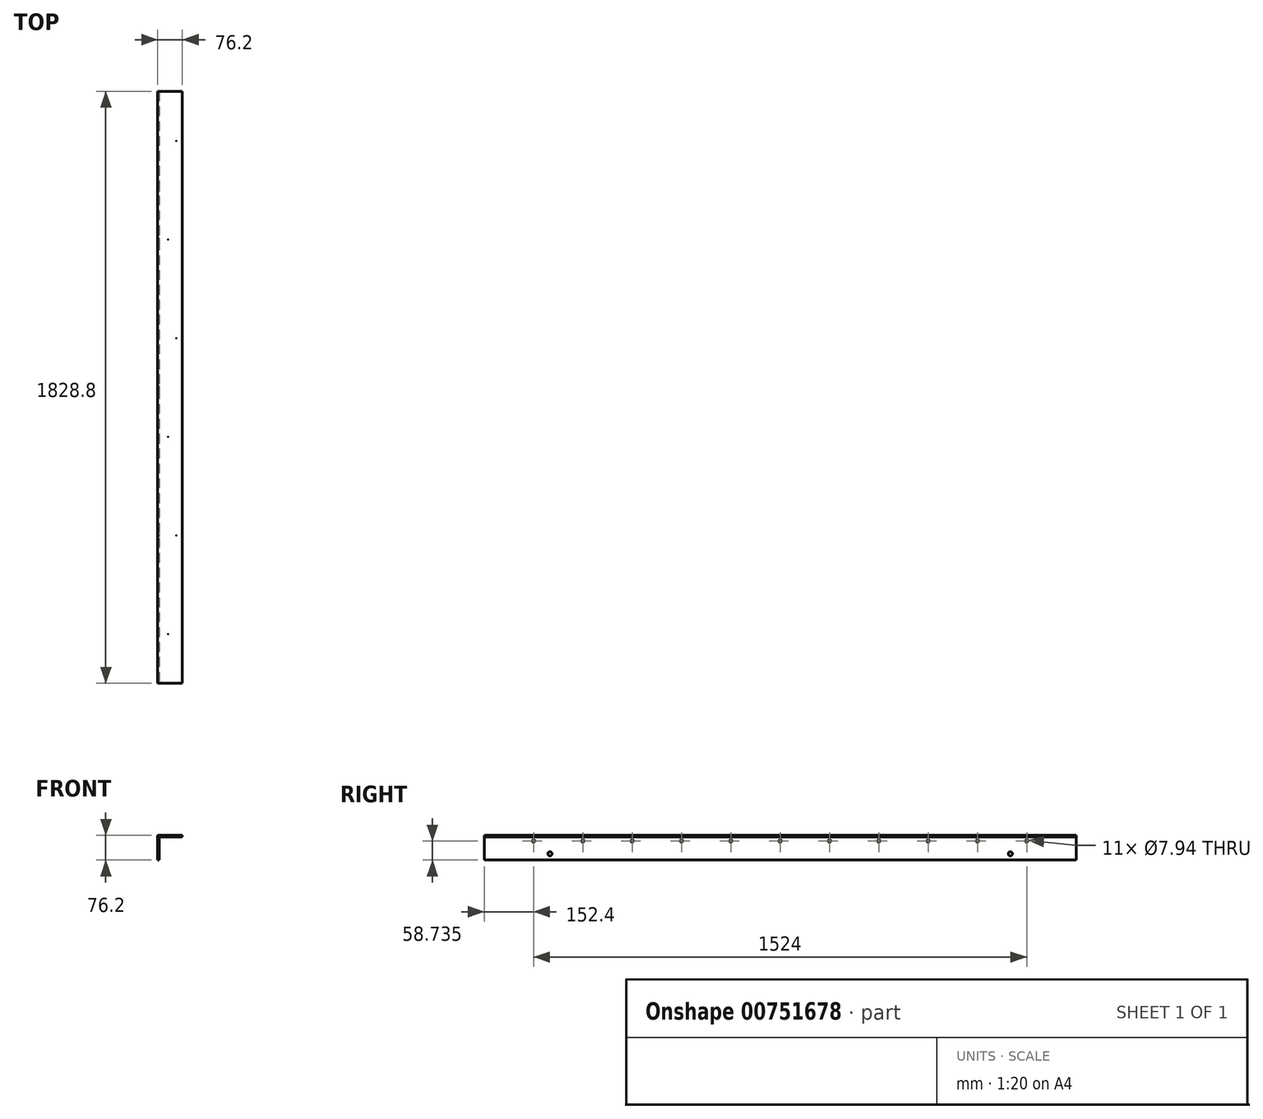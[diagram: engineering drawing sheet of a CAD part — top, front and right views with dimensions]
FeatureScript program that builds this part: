
annotation { "Feature Type Name" : "Feature", "Feature Type Description" : "" }
export const myFeature = defineFeature(function(context is Context, id is Id, definition is map)
    precondition{}
    {
        {
            var Q0;
            Q0=qCreatedBy(makeId("Front.planeOp"),FACE);
            var sketch = newSketch(context, id + "F0", { "sketchPlane" : qUnion([Q0])});
            skLineSegment(sketch, "E0", {"start": v(-59.9, 6.5) * mm, "end": v(16.3, 6.5) * mm});
            skLineSegment(sketch, "E1", {"start": v(16.3, 6.5) * mm, "end": v(16.3, 11.27) * mm});
            skLineSegment(sketch, "E2", {"start": v(16.3, 11.27) * mm, "end": v(-55.14, 11.27) * mm});
            skLineSegment(sketch, "E3", {"start": v(-55.14, 11.27) * mm, "end": v(-55.14, 82.7) * mm});
            skLineSegment(sketch, "E4", {"start": v(-55.14, 82.7) * mm, "end": v(-59.9, 82.7) * mm});
            skLineSegment(sketch, "E5", {"start": v(-59.9, 82.7) * mm, "end": v(-59.9, 6.5) * mm});
            skSolve(sketch);
        }
        {
            var Q0;
            Q0=makeQuery(id+"F0.imprint","IMPRINT",FACE,{"disambiguationData":[TD([[makeQuery(id+"F0.imprint","IMPRINT",EDGE,{"derivedFrom":sQuery(id+"F0.wireOp",EDGE,"E0")}),1.0]])]});
            var Q1;
            Q1=qSketchRegion(id+"F2",true);
            var Q2;
            Q2=qSketchRegion(id+"FxbZRgylOvMu3Zg_1",true);
            extrude(context, id + "F1", {"entities" : qUnion([Q0, Q1, Q2]), "depth" : 1828.8 * mm, "offsetDistance" : 25.4 * mm});
        }
        {
            var Q0;
            Q0=makeQuery(id+"F1.opExtrude","SWEPT_FACE",FACE,{"disambiguationData":[OSD([sQuery(id+"F0.wireOp",EDGE,"E3")])]});
            var sketch = newSketch(context, id + "F2", { "sketchPlane" : qUnion([Q0])});
            skPoint(sketch, "E6", {"position": v(-1625.6, 63.65) * mm});
            skPoint(sketch, "E7", {"position": v(-203.2, 63.65) * mm});
            skSolve(sketch);
        }
        {
            var Q0;
            Q0=sQuery(id+"F2.wireOp",VERTEX,"E7");
            var Q1;
            Q1=sQuery(id+"F2.wireOp",VERTEX,"E6");
            var Q2;
            Q2=makeQuery(id+"F1.opExtrude","SWEPT_BODY",BODY,{"disambiguationData":[OSD([sQuery(id+"F0.wireOp",EDGE,"E0"),sQuery(id+"F0.wireOp",EDGE,"E1"),sQuery(id+"F0.wireOp",EDGE,"E2"),sQuery(id+"F0.wireOp",EDGE,"E3"),sQuery(id+"F0.wireOp",EDGE,"E4"),sQuery(id+"F0.wireOp",EDGE,"E5")])]});
            hole(context, id + "F3", {"style" : HoleStyle.SIMPLE, "endStyle" : HoleEndStyle.THROUGH, "holeDiameter" : 12.7 * mm, "majorDiameter" : 6.35 * mm, "isTappedThrough" : true, "tappedDepth" : 12.7 * mm, "tapClearance" : 3, "locations" : qUnion([Q0, Q1]), "scope" : qUnion([Q2])});
        }
        {
            var Q0;
            Q0=qCreatedBy(makeId("Top.planeOp"),FACE);
            var sketch = newSketch(context, id + "F4", { "sketchPlane" : qUnion([Q0])});
            skPoint(sketch, "E8", {"position": v(0, 0) * mm});
            skPoint(sketch, "E9", {"position": v(-28.15, -152.4) * mm});
            skPoint(sketch, "E10", {"position": v(-28.15, -762) * mm});
            skPoint(sketch, "E11", {"position": v(-28.15, -1371.6) * mm});
            skPoint(sketch, "E12", {"position": v(-2.75, -1066.8) * mm});
            skPoint(sketch, "E13", {"position": v(-2.75, -1676.4) * mm});
            skPoint(sketch, "E14", {"position": v(-2.75, -457.2) * mm});
            skSolve(sketch);
        }
        {
            var Q0;
            Q0=sQuery(id+"F4.wireOp",VERTEX,"E11");
            var Q1;
            Q1=sQuery(id+"F4.wireOp",VERTEX,"E13");
            var Q2;
            Q2=sQuery(id+"F4.wireOp",VERTEX,"E12");
            var Q3;
            Q3=sQuery(id+"F4.wireOp",VERTEX,"E10");
            var Q4;
            Q4=sQuery(id+"F4.wireOp",VERTEX,"E14");
            var Q5;
            Q5=sQuery(id+"F4.wireOp",VERTEX,"E9");
            var Q6;
            Q6=makeQuery(id+"F1.opExtrude","SWEPT_BODY",BODY,{"disambiguationData":[OSD([sQuery(id+"F0.wireOp",EDGE,"E0"),sQuery(id+"F0.wireOp",EDGE,"E1"),sQuery(id+"F0.wireOp",EDGE,"E2"),sQuery(id+"F0.wireOp",EDGE,"E3"),sQuery(id+"F0.wireOp",EDGE,"E4"),sQuery(id+"F0.wireOp",EDGE,"E5")])]});
            hole(context, id + "F5", {"style" : HoleStyle.SIMPLE, "endStyle" : HoleEndStyle.THROUGH, "oppositeDirection" : true, "holeDiameter" : 3 / 203.2 * mm, "majorDiameter" : 6.35 * mm, "isTappedThrough" : true, "tappedDepth" : 12.7 * mm, "tapClearance" : 3, "locations" : qUnion([Q0, Q1, Q2, Q3, Q4, Q5]), "scope" : qUnion([Q6])});
        }
        {
            var Q0;
            Q0=makeQuery(id+"F1.opExtrude","SWEPT_BODY",BODY,{"disambiguationData":[OSD([sQuery(id+"F0.wireOp",EDGE,"E0"),sQuery(id+"F0.wireOp",EDGE,"E1"),sQuery(id+"F0.wireOp",EDGE,"E2"),sQuery(id+"F0.wireOp",EDGE,"E3"),sQuery(id+"F0.wireOp",EDGE,"E4"),sQuery(id+"F0.wireOp",EDGE,"E5")])]});
            var Q1;
            Q1=makeQuery(id+"F1.opExtrude","CAP_EDGE",EDGE,{"disambiguationData":[OSD([sQuery(id+"F0.wireOp",EDGE,"E2")])],"isStart":false});
            transform(context, id + "F6", {"entities" : qUnion([Q0]), "transformType" : TransformType.ROTATION, "transformAxis" : qUnion([Q1]), "angle" : 180 * degree, "makeCopy" : false});
        }
        {
            var Q0;
            Q0=makeQuery(id+"F1.opExtrude","SWEPT_BODY",BODY,{"disambiguationData":[OSD([sQuery(id+"F0.wireOp",EDGE,"E0"),sQuery(id+"F0.wireOp",EDGE,"E1"),sQuery(id+"F0.wireOp",EDGE,"E2"),sQuery(id+"F0.wireOp",EDGE,"E3"),sQuery(id+"F0.wireOp",EDGE,"E4"),sQuery(id+"F0.wireOp",EDGE,"E5")])]});
            transform(context, id + "F7", {"entities" : qUnion([Q0]), "transformType" : TransformType.TRANSLATION_3D, "dx" : 0 * mm, "dy" : 1828.8 * mm, "dz" : 0 * mm, "makeCopy" : false});
        }
        {
            var Q0;
            Q0=makeQuery(id+"F1.opExtrude","SWEPT_FACE",FACE,{"disambiguationData":[OSD([sQuery(id+"F0.wireOp",EDGE,"E3")])]});
            var sketch = newSketch(context, id + "F8", { "sketchPlane" : qUnion([Q0])});
            skPoint(sketch, "E15", {"position": v(-304.8, -1.43) * mm});
            skPoint(sketch, "E16", {"position": v(-457.2, -1.43) * mm});
            skPoint(sketch, "E17", {"position": v(-609.6, -1.43) * mm});
            skPoint(sketch, "E18", {"position": v(-762, -1.43) * mm});
            skPoint(sketch, "E19", {"position": v(-914.4, -1.43) * mm});
            skPoint(sketch, "E20", {"position": v(-1066.8, -1.43) * mm});
            skPoint(sketch, "E21", {"position": v(-1219.2, -1.43) * mm});
            skPoint(sketch, "E22", {"position": v(-1371.6, -1.43) * mm});
            skPoint(sketch, "E23", {"position": v(-1524, -1.43) * mm});
            skPoint(sketch, "E24", {"position": v(-1676.4, -1.43) * mm});
            skPoint(sketch, "E25", {"position": v(-152.4, -1.43) * mm});
            skSolve(sketch);
        }
        {
            var Q0;
            Q0=sQuery(id+"F8.wireOp",VERTEX,"E25");
            var Q1;
            Q1=sQuery(id+"F8.wireOp",VERTEX,"E15");
            var Q2;
            Q2=sQuery(id+"F8.wireOp",VERTEX,"E16");
            var Q3;
            Q3=sQuery(id+"F8.wireOp",VERTEX,"E17");
            var Q4;
            Q4=sQuery(id+"F8.wireOp",VERTEX,"E18");
            var Q5;
            Q5=sQuery(id+"F8.wireOp",VERTEX,"E19");
            var Q6;
            Q6=sQuery(id+"F8.wireOp",VERTEX,"E20");
            var Q7;
            Q7=sQuery(id+"F8.wireOp",VERTEX,"E21");
            var Q8;
            Q8=sQuery(id+"F8.wireOp",VERTEX,"E22");
            var Q9;
            Q9=sQuery(id+"F8.wireOp",VERTEX,"E23");
            var Q10;
            Q10=sQuery(id+"F8.wireOp",VERTEX,"E24");
            var Q11;
            Q11=makeQuery(id+"F1.opExtrude","SWEPT_BODY",BODY,{"disambiguationData":[OSD([sQuery(id+"F0.wireOp",EDGE,"E0"),sQuery(id+"F0.wireOp",EDGE,"E1"),sQuery(id+"F0.wireOp",EDGE,"E2"),sQuery(id+"F0.wireOp",EDGE,"E3"),sQuery(id+"F0.wireOp",EDGE,"E4"),sQuery(id+"F0.wireOp",EDGE,"E5")])]});
            hole(context, id + "F9", {"style" : HoleStyle.SIMPLE, "endStyle" : HoleEndStyle.THROUGH, "holeDiameter" : 7.94 * mm, "majorDiameter" : 6.35 * mm, "isTappedThrough" : true, "tappedDepth" : 12.7 * mm, "tapClearance" : 3, "locations" : qUnion([Q0, Q1, Q2, Q3, Q4, Q5, Q6, Q7, Q8, Q9, Q10]), "scope" : qUnion([Q11])});
        }
    });
